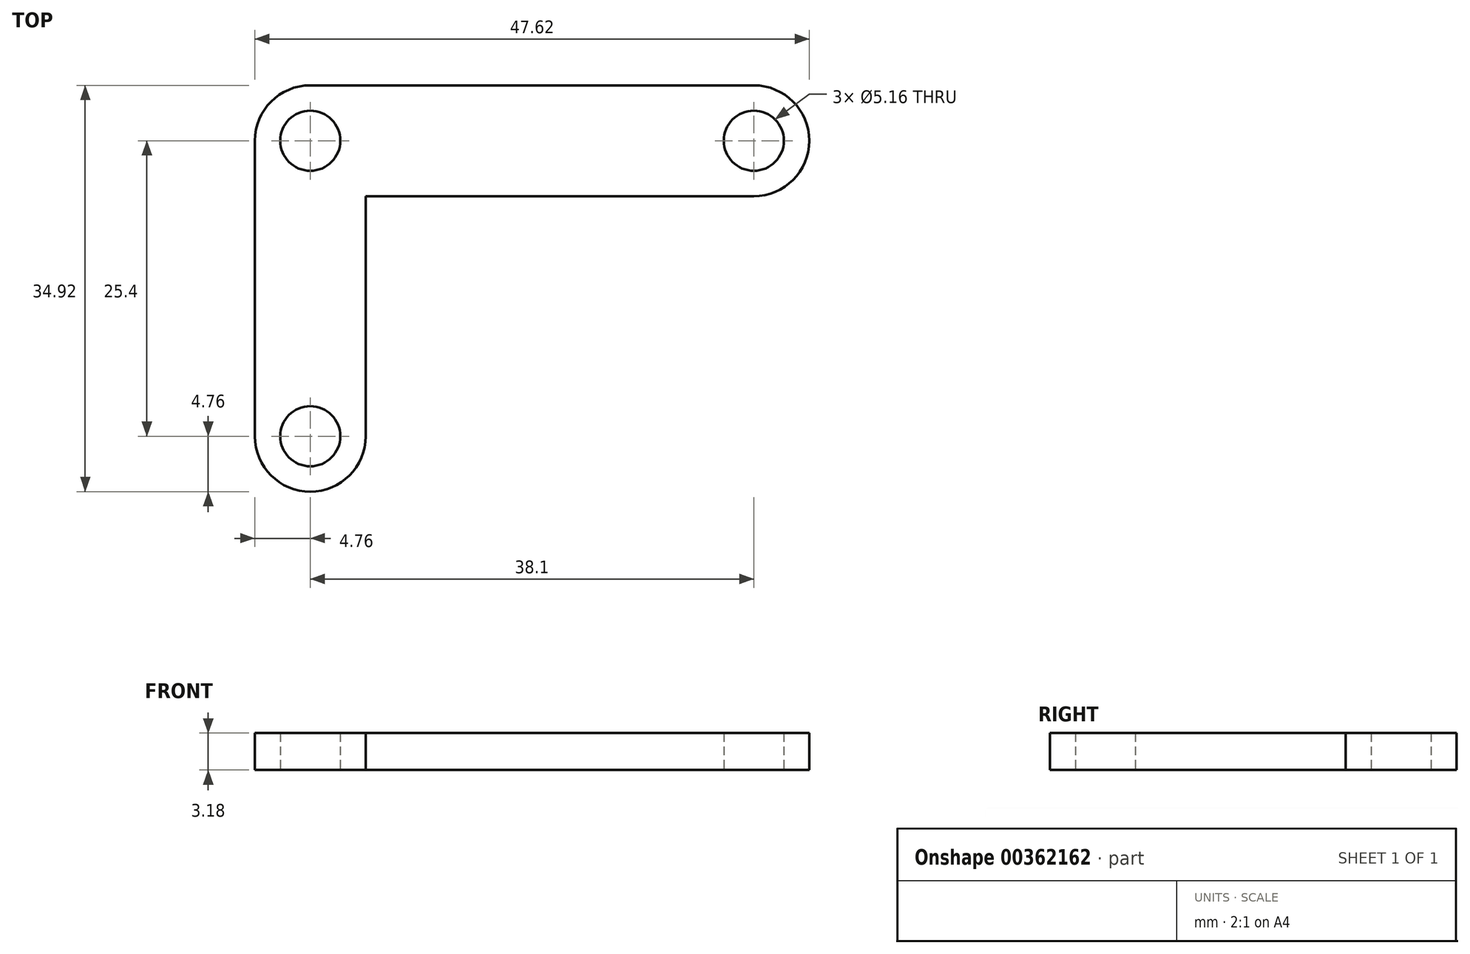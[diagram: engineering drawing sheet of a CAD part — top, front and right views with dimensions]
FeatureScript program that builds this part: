
annotation { "Feature Type Name" : "Feature", "Feature Type Description" : "" }
export const myFeature = defineFeature(function(context is Context, id is Id, definition is map)
    precondition{}
    {
        {
            var Q0;
            Q0=qCreatedBy(makeId("Top.planeOp"),FACE);
            var sketch = newSketch(context, id + "F0", { "sketchPlane" : qUnion([Q0])});
            skLineSegment(sketch, "E0", {"start": v(0, 0) * mm, "end": v(38.1, 0) * mm, "construction": true});
            skLineSegment(sketch, "E1", {"start": v(0, 0) * mm, "end": v(0, -25.4) * mm, "construction": true});
            skArc(sketch, "E2", {"start": v(-4.76, -25.4) * mm, "mid": v(0, -30.16) * mm, "end": v(4.76, -25.4) * mm});
            skArc(sketch, "E3", {"start": v(38.1, 4.76) * mm, "mid": v(42.86, 0) * mm, "end": v(38.1, -4.76) * mm});
            skArc(sketch, "E4", {"start": v(-4.76, 0) * mm, "mid": v(-3.37, 3.37) * mm, "end": v(0, 4.76) * mm});
            skLineSegment(sketch, "E5", {"start": v(-4.76, -25.4) * mm, "end": v(-4.76, 0) * mm});
            skLineSegment(sketch, "E6", {"start": v(0, 4.76) * mm, "end": v(38.1, 4.76) * mm});
            skLineSegment(sketch, "E7", {"start": v(38.1, -4.76) * mm, "end": v(4.76, -4.76) * mm});
            skLineSegment(sketch, "E8", {"start": v(4.76, -25.4) * mm, "end": v(4.76, -4.76) * mm});
            skSolve(sketch);
        }
        {
            var Q0;
            Q0=makeQuery(id+"F0.imprint","IMPRINT",FACE,{"disambiguationData":[TD([[makeQuery(id+"F0.imprint","IMPRINT",EDGE,{"derivedFrom":sQuery(id+"F0.wireOp",EDGE,"E2")}),1.0]])]});
            extrude(context, id + "F1", {"entities" : qUnion([Q0]), "depth" : 3.17 * mm, "offsetDistance" : 25.4 * mm});
        }
        {
            var Q0;
            Q0=sQuery(id+"F0.wireOp",VERTEX,"E2.center");
            var Q1;
            Q1=sQuery(id+"F0.wireOp",VERTEX,"E4.center");
            var Q2;
            Q2=sQuery(id+"F0.wireOp",VERTEX,"E0.end");
            var Q3;
            Q3=makeQuery(id+"F1.opExtrude","SWEPT_BODY",BODY,{"disambiguationData":[OSD([sQuery(id+"F0.wireOp",EDGE,"E2"),sQuery(id+"F0.wireOp",EDGE,"E3"),sQuery(id+"F0.wireOp",EDGE,"E4"),sQuery(id+"F0.wireOp",EDGE,"E5"),sQuery(id+"F0.wireOp",EDGE,"E6"),sQuery(id+"F0.wireOp",EDGE,"E7"),sQuery(id+"F0.wireOp",EDGE,"E8")])]});
            hole(context, id + "F2", {"style" : HoleStyle.SIMPLE, "endStyle" : HoleEndStyle.THROUGH, "oppositeDirection" : true, "holeDiameter" : 5.16 * mm, "isTappedThrough" : true, "tappedDepth" : 12.7 * mm, "tapClearance" : 3, "startFromSketch" : true, "locations" : qUnion([Q0, Q1, Q2]), "scope" : qUnion([Q3])});
        }
    });
